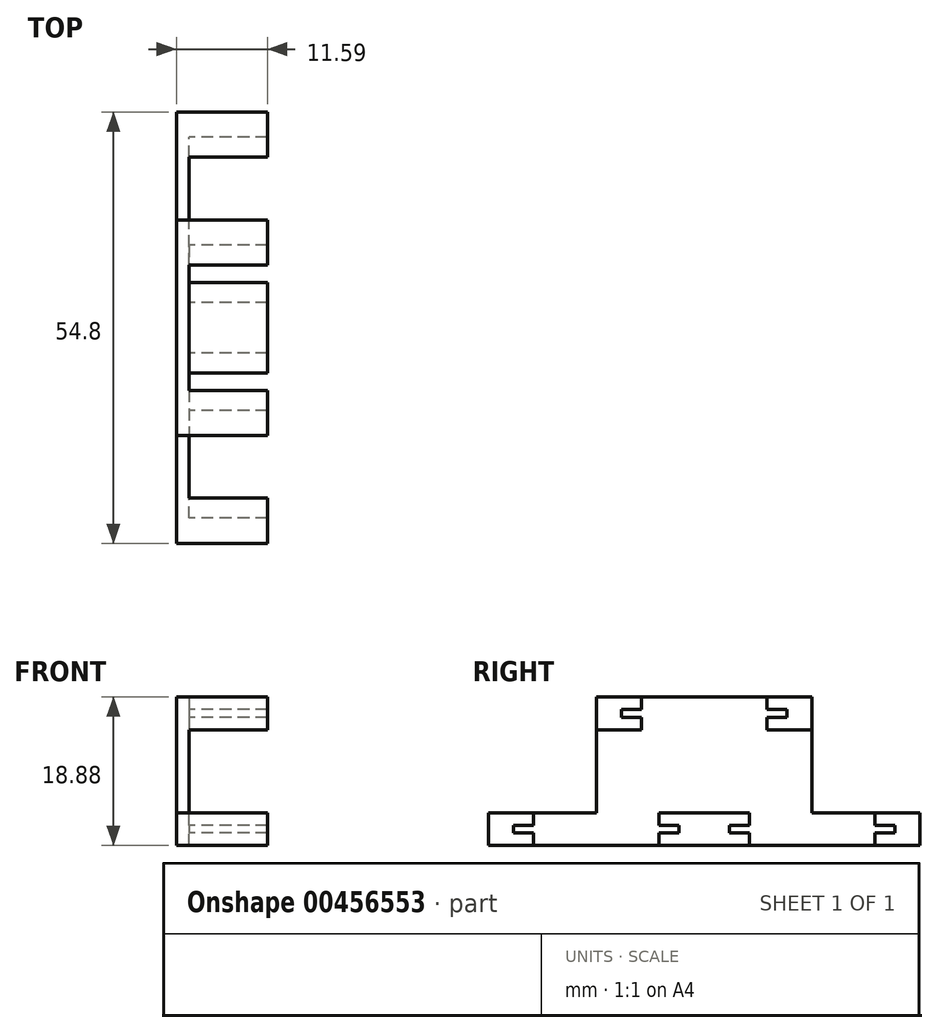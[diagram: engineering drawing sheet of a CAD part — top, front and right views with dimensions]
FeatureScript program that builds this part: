
annotation { "Feature Type Name" : "Feature", "Feature Type Description" : "" }
export const myFeature = defineFeature(function(context is Context, id is Id, definition is map)
    precondition{}
    {
        {
            var Q0;
            Q0=qCreatedBy(makeId("Right.planeOp"),FACE);
            var sketch = newSketch(context, id + "F0", { "sketchPlane" : qUnion([Q0])});
            skLineSegment(sketch, "E0.bottom", {"start": v(-10.5, 15.2) * mm, "end": v(10.5, 15.2) * mm});
            skLineSegment(sketch, "E0.top", {"start": v(-10.5, 14.2) * mm, "end": v(10.5, 14.2) * mm});
            skLineSegment(sketch, "E0.left", {"start": v(-10.5, 15.2) * mm, "end": v(-10.5, 14.2) * mm});
            skLineSegment(sketch, "E0.right", {"start": v(10.5, 15.2) * mm, "end": v(10.5, 14.2) * mm});
            skPoint(sketch, "E0.middle", {"position": v(0, 14.7) * mm});
            skLineSegment(sketch, "E1.bottom", {"start": v(-24.2, 0.5) * mm, "end": v(-3.2, 0.5) * mm});
            skLineSegment(sketch, "E1.top", {"start": v(-24.2, -0.5) * mm, "end": v(-3.2, -0.5) * mm});
            skLineSegment(sketch, "E1.left", {"start": v(-24.2, 0.5) * mm, "end": v(-24.2, -0.5) * mm});
            skLineSegment(sketch, "E1.right", {"start": v(-3.2, 0.5) * mm, "end": v(-3.2, -0.5) * mm});
            skPoint(sketch, "E1.middle", {"position": v(-13.7, 0) * mm});
            skLineSegment(sketch, "E2.bottom", {"start": v(3.2, 0.5) * mm, "end": v(24.2, 0.5) * mm});
            skLineSegment(sketch, "E2.top", {"start": v(3.2, -0.5) * mm, "end": v(24.2, -0.5) * mm});
            skLineSegment(sketch, "E2.left", {"start": v(3.2, 0.5) * mm, "end": v(3.2, -0.5) * mm});
            skLineSegment(sketch, "E2.right", {"start": v(24.2, 0.5) * mm, "end": v(24.2, -0.5) * mm});
            skPoint(sketch, "E2.middle", {"position": v(13.7, 0) * mm});
            skLineSegment(sketch, "E3", {"start": v(-13.7, 0) * mm, "end": v(0, 0) * mm, "construction": true});
            skLineSegment(sketch, "E4", {"start": v(0, 0) * mm, "end": v(13.7, 0) * mm, "construction": true});
            skLineSegment(sketch, "E5", {"start": v(-13.7, 0.5) * mm, "end": v(0, 14.2) * mm});
            skLineSegment(sketch, "E6", {"start": v(0, 14.2) * mm, "end": v(13.7, 0.5) * mm});
            skLineSegment(sketch, "E7", {"start": v(-13.7, 0.5) * mm, "end": v(0, -13.2) * mm});
            skLineSegment(sketch, "E8", {"start": v(0, -13.2) * mm, "end": v(13.7, 0.5) * mm});
            skLineSegment(sketch, "E9", {"start": v(-13.7, 0.5) * mm, "end": v(-27.4, 14.2) * mm});
            skLineSegment(sketch, "E10", {"start": v(13.7, 0.5) * mm, "end": v(27.4, 14.2) * mm});
            skSolve(sketch);
        }
        {
            var Q0;
            Q0=qCreatedBy(makeId("Right.planeOp"),FACE);
            var sketch = newSketch(context, id + "F1", { "sketchPlane" : qUnion([Q0])});
            skLineSegment(sketch, "E11.0", {"start": v(-10.5, 15.2) * mm, "end": v(-10.5, 14.2) * mm});
            skLineSegment(sketch, "E11.1", {"start": v(10.5, 15.2) * mm, "end": v(10.5, 14.2) * mm});
            skLineSegment(sketch, "E11.2", {"start": v(-24.2, 0.5) * mm, "end": v(-24.2, -0.5) * mm});
            skLineSegment(sketch, "E11.3", {"start": v(-3.2, 0.5) * mm, "end": v(-3.2, -0.5) * mm});
            skLineSegment(sketch, "E11.4", {"start": v(3.2, 0.5) * mm, "end": v(3.2, -0.5) * mm});
            skLineSegment(sketch, "E11.5", {"start": v(24.2, 0.5) * mm, "end": v(24.2, -0.5) * mm});
            skLineSegment(sketch, "E12", {"start": v(-10.5, 14.2) * mm, "end": v(-7.96, 14.2) * mm});
            skLineSegment(sketch, "E13", {"start": v(-7.96, 14.2) * mm, "end": v(-7.96, 12.61) * mm});
            skLineSegment(sketch, "E14", {"start": v(-7.96, 12.61) * mm, "end": v(-13.7, 12.61) * mm});
            skLineSegment(sketch, "E15", {"start": v(-13.7, 12.61) * mm, "end": v(-13.7, 16.79) * mm});
            skLineSegment(sketch, "E16", {"start": v(-13.7, 16.79) * mm, "end": v(-7.96, 16.79) * mm});
            skLineSegment(sketch, "E17", {"start": v(-7.96, 16.79) * mm, "end": v(-7.96, 15.2) * mm});
            skLineSegment(sketch, "E18", {"start": v(-7.96, 15.2) * mm, "end": v(-10.5, 15.2) * mm});
            skLineSegment(sketch, "E19", {"start": v(-3.2, 0.5) * mm, "end": v(-5.74, 0.5) * mm});
            skLineSegment(sketch, "E20", {"start": v(-5.74, 0.5) * mm, "end": v(-5.74, 2.09) * mm});
            skLineSegment(sketch, "E21", {"start": v(-5.74, 2.09) * mm, "end": v(0, 2.09) * mm});
            skLineSegment(sketch, "E22", {"start": v(0, 2.09) * mm, "end": v(0, -2.09) * mm});
            skLineSegment(sketch, "E23", {"start": v(0, -2.09) * mm, "end": v(-5.74, -2.09) * mm});
            skLineSegment(sketch, "E24", {"start": v(-5.74, -2.09) * mm, "end": v(-5.74, -0.5) * mm});
            skLineSegment(sketch, "E25", {"start": v(-5.74, -0.5) * mm, "end": v(-3.2, -0.5) * mm});
            skLineSegment(sketch, "E26", {"start": v(-24.2, 0.5) * mm, "end": v(-21.66, 0.5) * mm});
            skLineSegment(sketch, "E27", {"start": v(-21.66, 0.5) * mm, "end": v(-21.66, 2.09) * mm});
            skLineSegment(sketch, "E28", {"start": v(-21.66, 2.09) * mm, "end": v(-27.4, 2.09) * mm});
            skLineSegment(sketch, "E29", {"start": v(-27.4, 2.09) * mm, "end": v(-27.4, -2.09) * mm});
            skLineSegment(sketch, "E30", {"start": v(-27.4, -2.09) * mm, "end": v(-21.66, -2.09) * mm});
            skLineSegment(sketch, "E31", {"start": v(-21.66, -2.09) * mm, "end": v(-21.66, -0.5) * mm});
            skLineSegment(sketch, "E32", {"start": v(-21.66, -0.5) * mm, "end": v(-24.2, -0.5) * mm});
            skSolve(sketch);
        }
        {
            var Q0;
            Q0 = qSketchRegion(id + "F1", true);
            extrude(context, id + "F2", {"entities" : qUnion([Q0]), "depth" : 10 * mm});
        }
        {
            var Q0;
            Q0=makeQuery(id+"F2.opExtrude","SWEPT_BODY",BODY,{"disambiguationData":[OSD([sQuery(id+"F1.wireOp",EDGE,"E11.2"),sQuery(id+"F1.wireOp",EDGE,"E26"),sQuery(id+"F1.wireOp",EDGE,"E27"),sQuery(id+"F1.wireOp",EDGE,"E28"),sQuery(id+"F1.wireOp",EDGE,"E29"),sQuery(id+"F1.wireOp",EDGE,"E30"),sQuery(id+"F1.wireOp",EDGE,"E31"),sQuery(id+"F1.wireOp",EDGE,"E32")])]});
            var Q1;
            Q1=makeQuery(id+"F2.opExtrude","SWEPT_BODY",BODY,{"disambiguationData":[OSD([sQuery(id+"F1.wireOp",EDGE,"E11.3"),sQuery(id+"F1.wireOp",EDGE,"E19"),sQuery(id+"F1.wireOp",EDGE,"E20"),sQuery(id+"F1.wireOp",EDGE,"E21"),sQuery(id+"F1.wireOp",EDGE,"E22"),sQuery(id+"F1.wireOp",EDGE,"E23"),sQuery(id+"F1.wireOp",EDGE,"E24"),sQuery(id+"F1.wireOp",EDGE,"E25")])]});
            var Q2;
            Q2=makeQuery(id+"F2.opExtrude","SWEPT_BODY",BODY,{"disambiguationData":[OSD([sQuery(id+"F1.wireOp",EDGE,"E11.0"),sQuery(id+"F1.wireOp",EDGE,"E12"),sQuery(id+"F1.wireOp",EDGE,"E13"),sQuery(id+"F1.wireOp",EDGE,"E14"),sQuery(id+"F1.wireOp",EDGE,"E15"),sQuery(id+"F1.wireOp",EDGE,"E16"),sQuery(id+"F1.wireOp",EDGE,"E17"),sQuery(id+"F1.wireOp",EDGE,"E18")])]});
            var Q3;
            Q3=qCreatedBy(makeId("Front.planeOp"),FACE);
            mirror(context, id + "F3", {"entities" : qUnion([Q0, Q1, Q2]), "mirrorPlane" : qUnion([Q3])});
        }
        {
            var Q0;
            Q0=makeQuery(id+"F3.opPattern","COPY",FACE,{"derivedFrom":makeQuery(id+"F2.opExtrude","CAP_FACE",FACE,{"disambiguationData":[OSD([sQuery(id+"F1.wireOp",EDGE,"E11.0"),sQuery(id+"F1.wireOp",EDGE,"E12"),sQuery(id+"F1.wireOp",EDGE,"E13"),sQuery(id+"F1.wireOp",EDGE,"E14"),sQuery(id+"F1.wireOp",EDGE,"E15"),sQuery(id+"F1.wireOp",EDGE,"E16"),sQuery(id+"F1.wireOp",EDGE,"E17"),sQuery(id+"F1.wireOp",EDGE,"E18")])],"isStart":true}),"instanceName":"1"});
            var sketch = newSketch(context, id + "F4", { "sketchPlane" : qUnion([Q0])});
            skLineSegment(sketch, "E33", {"start": v(-13.7, 16.79) * mm, "end": v(-13.7, 2.09) * mm});
            skLineSegment(sketch, "E34", {"start": v(-13.7, 2.09) * mm, "end": v(-27.4, 2.09) * mm});
            skLineSegment(sketch, "E35", {"start": v(-27.4, 2.09) * mm, "end": v(-27.4, -2.09) * mm});
            skLineSegment(sketch, "E36", {"start": v(-27.4, -2.09) * mm, "end": v(27.4, -2.09) * mm});
            skLineSegment(sketch, "E37", {"start": v(27.4, -2.09) * mm, "end": v(27.4, 2.09) * mm});
            skLineSegment(sketch, "E38", {"start": v(27.4, 2.09) * mm, "end": v(13.7, 2.09) * mm});
            skLineSegment(sketch, "E39", {"start": v(13.7, 2.09) * mm, "end": v(13.7, 16.79) * mm});
            skLineSegment(sketch, "E40", {"start": v(13.7, 16.79) * mm, "end": v(-13.7, 16.79) * mm});
            skSolve(sketch);
        }
        {
            var Q0;
            Q0 = qSketchRegion(id + "F4", true);
            extrude(context, id + "F5", {"entities" : qUnion([Q0]), "operationType" : NewBodyOperationType.ADD, "depth" : 1.59 * mm});
        }
    });
